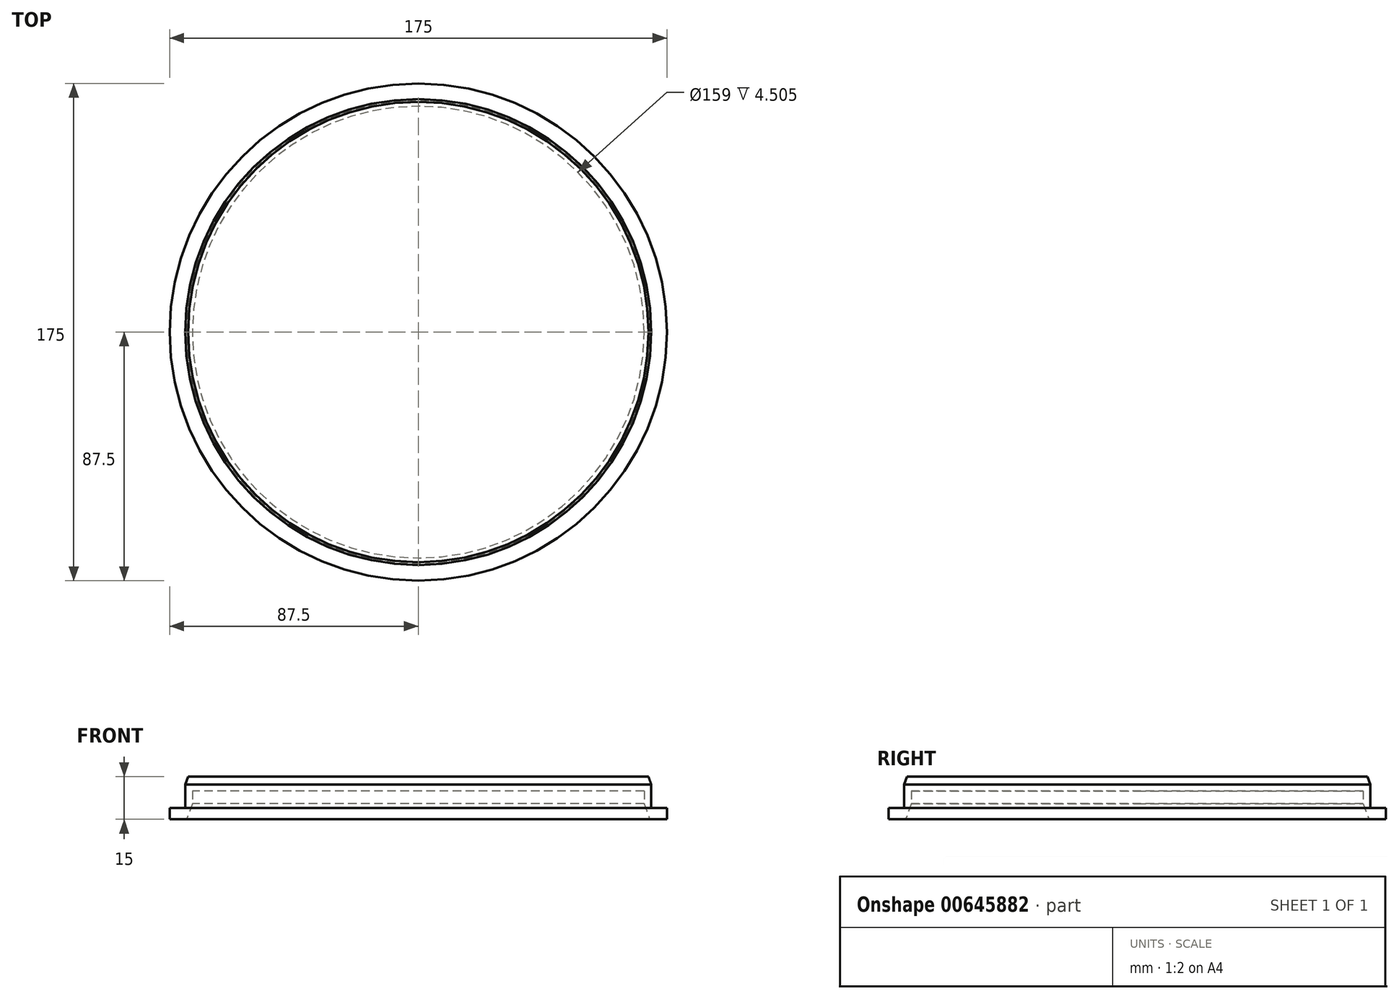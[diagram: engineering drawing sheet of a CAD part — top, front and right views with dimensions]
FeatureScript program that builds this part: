
annotation { "Feature Type Name" : "Feature", "Feature Type Description" : "" }
export const myFeature = defineFeature(function(context is Context, id is Id, definition is map)
    precondition{}
    {
        {
            var Q0;
            Q0=qCreatedBy(makeId("Top.planeOp"),FACE);
            var sketch = newSketch(context, id + "F0", { "sketchPlane" : qUnion([Q0])});
            skCircle(sketch, "E0", {"center": v(0, 0) * mm, "radius": 79.5 * mm});
            skCircle(sketch, "E1", {"center": v(0, 0) * mm, "radius": 82 * mm});
            skCircle(sketch, "E2", {"center": v(0, 0) * mm, "radius": 87.5 * mm});
            skSolve(sketch);
        }
        {
            var Q0;
            Q0=makeQuery(id+"F0.imprint","IMPRINT",FACE,{"disambiguationData":[TD([[makeQuery(id+"F0.imprint","IMPRINT",EDGE,{"derivedFrom":sQuery(id+"F0.wireOp",EDGE,"E0")}),1.0]])]});
            extrude(context, id + "F1", {"entities" : qUnion([Q0]), "depth" : 15 * mm, "offsetDistance" : 25 * mm, "hasSecondDirection" : true, "secondDirectionOppositeDirection" : false, "secondDirectionDepth" : 10 * mm});
        }
        {
            var Q0;
            Q0=makeQuery(id+"F0.imprint","IMPRINT",FACE,{"disambiguationData":[TD([[makeQuery(id+"F0.imprint","IMPRINT",EDGE,{"derivedFrom":sQuery(id+"F0.wireOp",EDGE,"E0")}),-1.0]])]});
            extrude(context, id + "F2", {"entities" : qUnion([Q0]), "operationType" : NewBodyOperationType.ADD, "depth" : 15 * mm, "offsetDistance" : 25 * mm});
        }
        {
            var Q0;
            Q0=makeQuery(id+"F0.imprint","IMPRINT",FACE,{"disambiguationData":[TD([[makeQuery(id+"F0.imprint","IMPRINT",EDGE,{"derivedFrom":sQuery(id+"F0.wireOp",EDGE,"E1")}),-1.0]])]});
            extrude(context, id + "F3", {"entities" : qUnion([Q0]), "operationType" : NewBodyOperationType.ADD, "depth" : 4 * mm, "offsetDistance" : 25 * mm});
        }
        {
            var Q0;
            Q0=makeQuery(id+"F2.opExtrude","CAP_EDGE",EDGE,{"disambiguationData":[OSD([sQuery(id+"F0.wireOp",EDGE,"E1")])],"isStart":false});
            chamfer(context, id + "F4", {"entities" : qUnion([Q0]), "chamferType" : ChamferType.OFFSET_ANGLE, "width" : 1 * mm, "oppositeDirection" : false, "angle" : 70 * degree, "tangentPropagation" : true});
        }
        {
            var Q0;
            Q0=makeQuery(id+"F2.opExtrude","CAP_EDGE",EDGE,{"disambiguationData":[OSD([sQuery(id+"F0.wireOp",EDGE,"E0")])],"isStart":true});
            chamfer(context, id + "F5", {"entities" : qUnion([Q0]), "chamferType" : ChamferType.OFFSET_ANGLE, "width" : 2 * mm, "oppositeDirection" : false, "angle" : 70 * degree, "tangentPropagation" : true});
        }
    });
